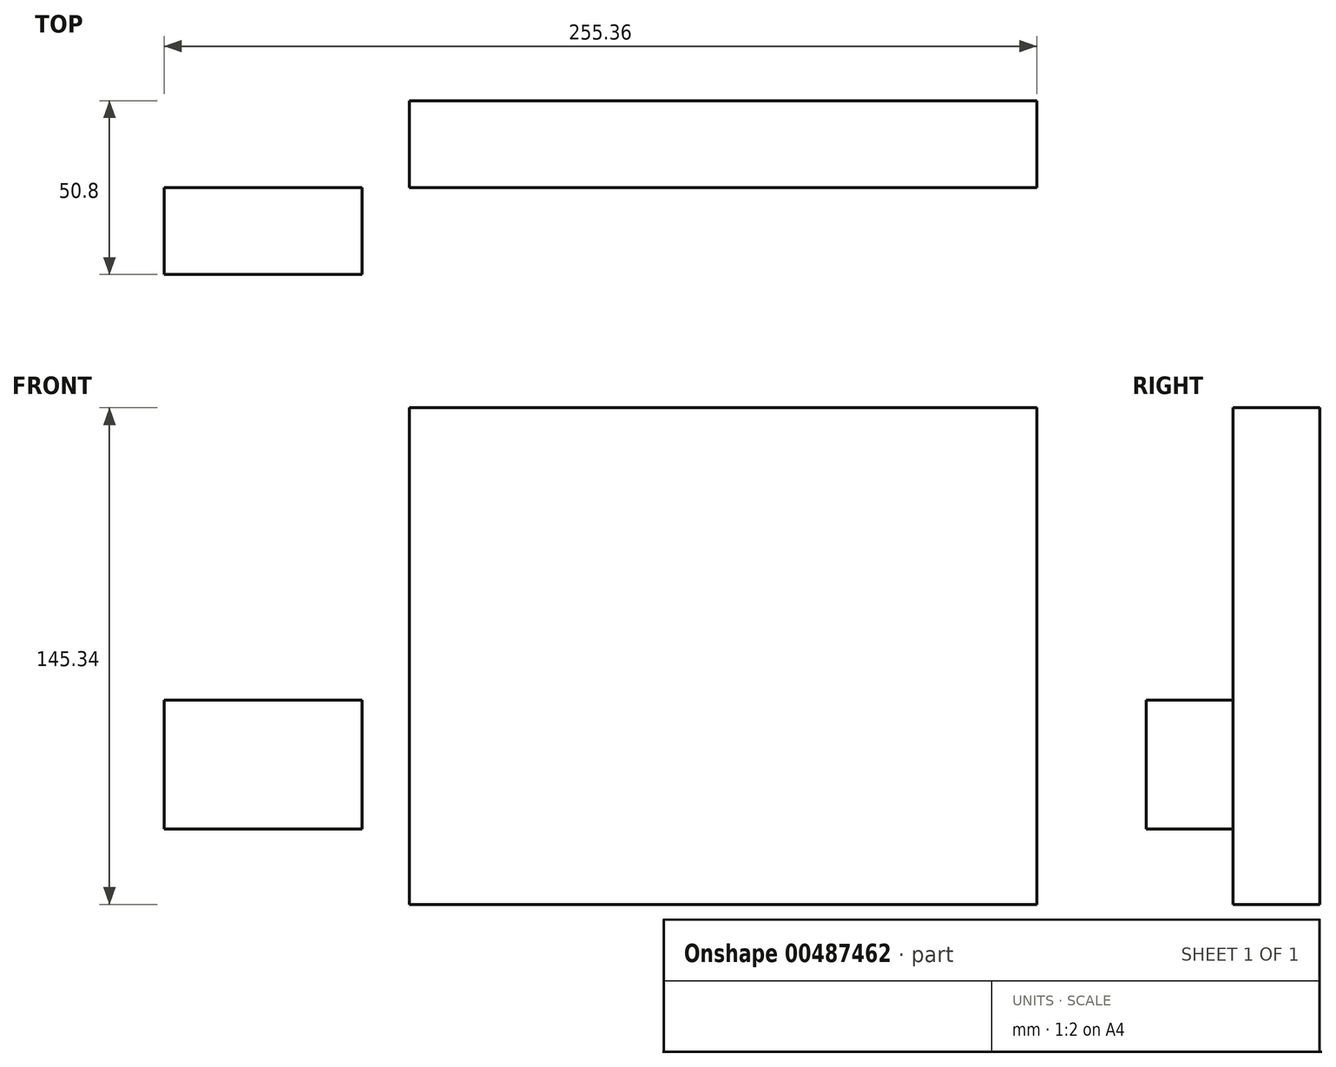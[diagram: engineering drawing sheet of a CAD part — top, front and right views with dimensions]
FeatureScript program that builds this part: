
annotation { "Feature Type Name" : "Feature", "Feature Type Description" : "" }
export const myFeature = defineFeature(function(context is Context, id is Id, definition is map)
    precondition{}
    {
        {
            var Q0;
            Q0=qCreatedBy(makeId("Front.planeOp"),FACE);
            var sketch = newSketch(context, id + "F0", { "sketchPlane" : qUnion([Q0])});
            skLineSegment(sketch, "E0.bottom", {"start": v(-107.52, 95.87) * mm, "end": v(76.1, 95.87) * mm});
            skLineSegment(sketch, "E0.top", {"start": v(-107.52, -49.47) * mm, "end": v(76.1, -49.47) * mm});
            skLineSegment(sketch, "E0.left", {"start": v(-107.52, 95.87) * mm, "end": v(-107.52, -49.47) * mm});
            skLineSegment(sketch, "E0.right", {"start": v(76.1, 95.87) * mm, "end": v(76.1, -49.47) * mm});
            skSolve(sketch);
        }
        {
            var Q0;
            Q0=makeQuery(id+"F0.imprint","IMPRINT",FACE,{"disambiguationData":[TD([[makeQuery(id+"F0.imprint","IMPRINT",EDGE,{"derivedFrom":sQuery(id+"F0.wireOp",EDGE,"E0.bottom")}),-1.0]])]});
            extrude(context, id + "F1", {"entities" : qUnion([Q0]), "depth" : 25.4 * mm});
        }
        {
            var Q0;
            Q0=makeQuery(id+"F1.opExtrude","CAP_FACE",FACE,{"disambiguationData":[OSD([sQuery(id+"F0.wireOp",EDGE,"E0.bottom"),sQuery(id+"F0.wireOp",EDGE,"E0.top"),sQuery(id+"F0.wireOp",EDGE,"E0.left"),sQuery(id+"F0.wireOp",EDGE,"E0.right")])],"isStart":false});
            var sketch = newSketch(context, id + "F2", { "sketchPlane" : qUnion([Q0])});
            skLineSegment(sketch, "E1.bottom", {"start": v(-179.26, 10.3) * mm, "end": v(-121.33, 10.3) * mm});
            skLineSegment(sketch, "E1.top", {"start": v(-179.26, -27.48) * mm, "end": v(-121.33, -27.48) * mm});
            skLineSegment(sketch, "E1.left", {"start": v(-179.26, 10.3) * mm, "end": v(-179.26, -27.48) * mm});
            skLineSegment(sketch, "E1.right", {"start": v(-121.33, 10.3) * mm, "end": v(-121.33, -27.48) * mm});
            skSolve(sketch);
        }
        {
            var Q0;
            Q0=makeQuery(id+"F2.imprint","IMPRINT",FACE,{"disambiguationData":[TD([[makeQuery(id+"F2.imprint","IMPRINT",EDGE,{"derivedFrom":sQuery(id+"F2.wireOp",EDGE,"E1.bottom")}),-1.0]])]});
            extrude(context, id + "F3", {"entities" : qUnion([Q0]), "depth" : 25.4 * mm});
        }
        {
            var Q0;
            Q0=makeQuery(id+"F1.opExtrude","CAP_FACE",FACE,{"disambiguationData":[OSD([sQuery(id+"F0.wireOp",EDGE,"E0.bottom"),sQuery(id+"F0.wireOp",EDGE,"E0.top"),sQuery(id+"F0.wireOp",EDGE,"E0.left"),sQuery(id+"F0.wireOp",EDGE,"E0.right")])],"isStart":true});
            var Q1;
            Q1=makeQuery(id+"F1.opExtrude","CAP_FACE",FACE,{"disambiguationData":[OSD([sQuery(id+"F0.wireOp",EDGE,"E0.bottom"),sQuery(id+"F0.wireOp",EDGE,"E0.top"),sQuery(id+"F0.wireOp",EDGE,"E0.left"),sQuery(id+"F0.wireOp",EDGE,"E0.right")])],"isStart":false});
            cPlane(context, id + "F4", {"entities" : qUnion([Q0, Q1]), "cplaneType" : CPlaneType.MID_PLANE, "offset" : 25.4 * mm, "width" : 152.4 * mm, "height" : 152.4 * mm});
        }
    });
